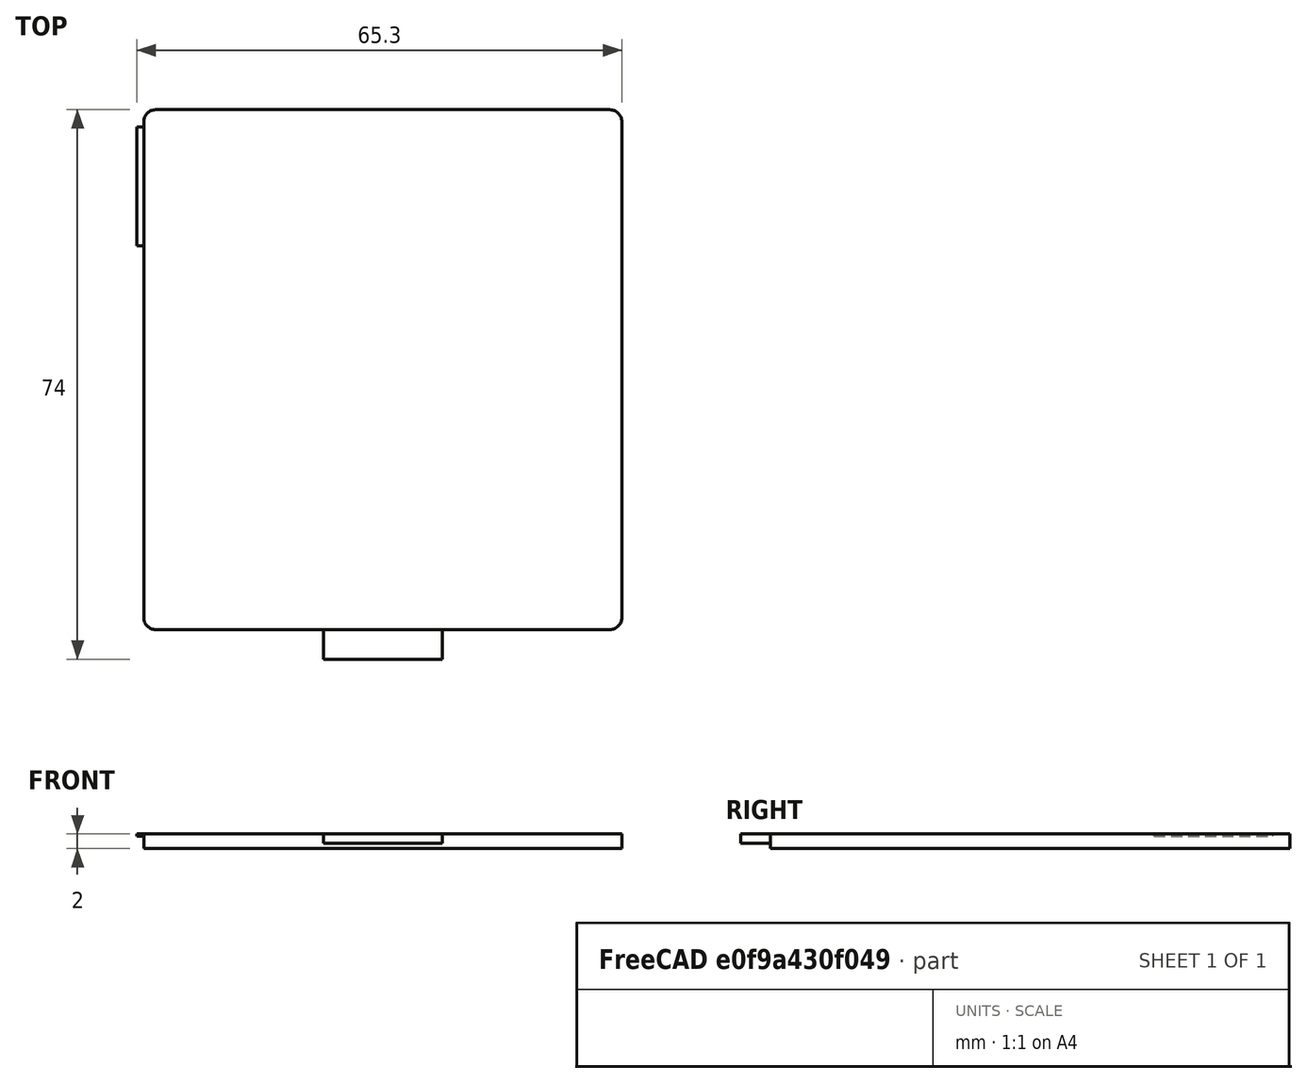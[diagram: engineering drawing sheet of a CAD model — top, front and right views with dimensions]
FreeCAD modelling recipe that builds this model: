
FCSTD DOCUMENT  (FreeCAD 0.21R33771 (Git))
Label: easy-battery-lid
License: All rights reserved
LicenseURL: http://en.wikipedia.org/wiki/All_rights_reserved
objects: Part::Box×3, Part::Fillet×1, Part::Mirroring×1
note: 5 computed .brp shape members not serialized (recipe doc carries the construction recipe); baked Part::Feature solids carry a one-line shape summary decoded from their .brp

FEATURE [Part::Box] Box  label="Cube"
  AttacherType = Attacher::AttachEngine3D
  Height = 2
  Length = 64.4
  Placement = pos=(-32.2,0,0) rot=(0,0,1;0rad)
  Width = 70
FEATURE [Part::Box] Box001  label="Cube001"
  AttacherType = Attacher::AttachEngine3D
  Height = 1.3
  Length = 16
  Placement = pos=(-8,-4,0.7) rot=(0,0,1;0rad)
  Width = 4
FEATURE [Part::Box] Box002  label="Cube002"
  AttacherType = Attacher::AttachEngine3D
  Height = 0.3
  Length = 0.9
  Placement = pos=(32.2,51.7,1.7) rot=(0,0,1;0rad)
  Width = 16
FEATURE [Part::Fillet] Fillet
  Base = -> Box
  Edges = 4 edges r=1.6: [Edge1,Edge3,Edge5,Edge7]
FEATURE [Part::Mirroring] Part__Mirroring  label="Cube002 (Mirror #1)"
  Base = (0,0,0)
  Normal = (1,0,0)
  Source = -> Box002
